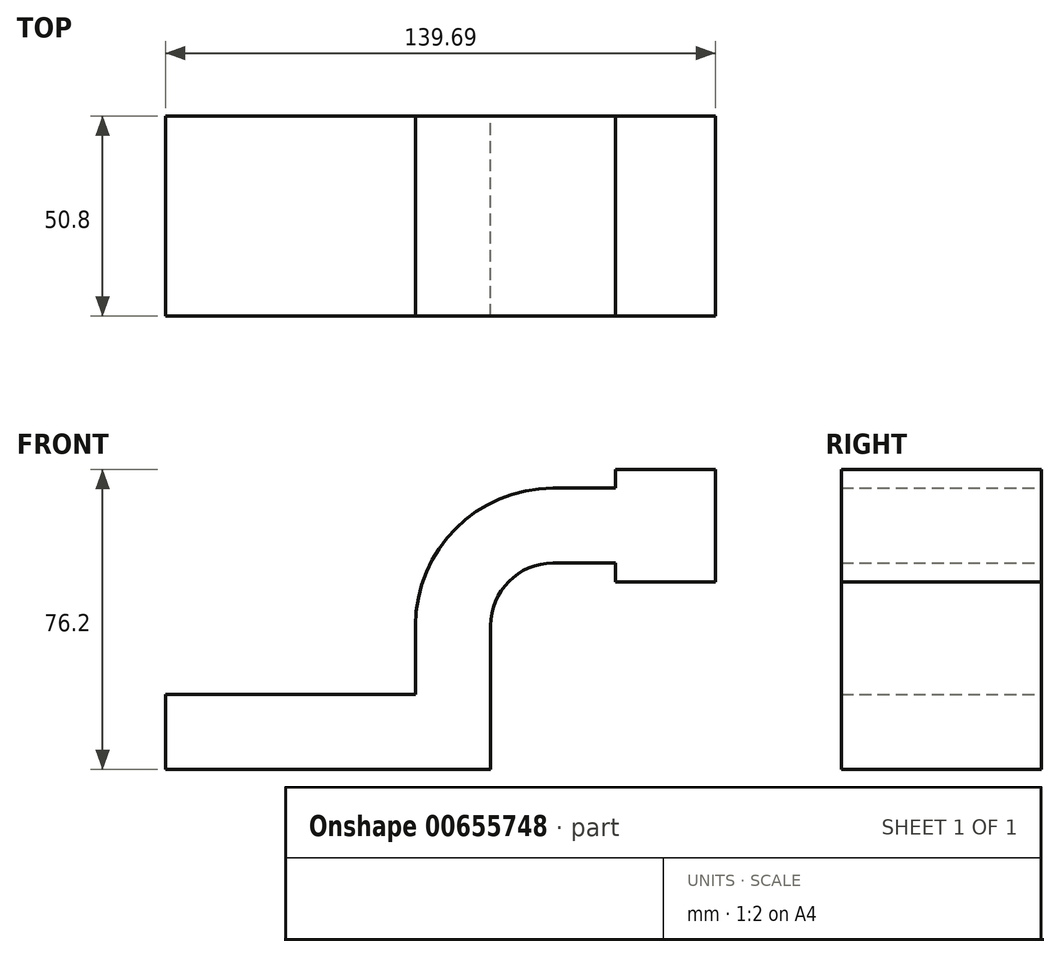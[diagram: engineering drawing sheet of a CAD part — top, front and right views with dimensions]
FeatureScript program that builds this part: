
annotation { "Feature Type Name" : "Feature", "Feature Type Description" : "" }
export const myFeature = defineFeature(function(context is Context, id is Id, definition is map)
    precondition{}
    {
        {
            var Q0;
            Q0=qCreatedBy(makeId("Front.planeOp"),FACE);
            var sketch = newSketch(context, id + "F0", { "sketchPlane" : qUnion([Q0])});
            skLineSegment(sketch, "E0.bottom", {"start": v(41.28, -9.52) * mm, "end": v(-41.28, -9.53) * mm});
            skLineSegment(sketch, "E0.top", {"start": v(41.28, 9.53) * mm, "end": v(-41.28, 9.53) * mm});
            skLineSegment(sketch, "E0.left", {"start": v(41.28, -9.52) * mm, "end": v(41.28, 9.53) * mm});
            skLineSegment(sketch, "E0.right", {"start": v(-41.28, -9.53) * mm, "end": v(-41.28, 9.53) * mm});
            skPoint(sketch, "E0.middle", {"position": v(0, 0) * mm});
            skLineSegment(sketch, "E1.bottom", {"start": v(98.43, 38.1) * mm, "end": v(73.03, 38.1) * mm});
            skLineSegment(sketch, "E1.top", {"start": v(98.43, 66.68) * mm, "end": v(73.03, 66.68) * mm});
            skLineSegment(sketch, "E1.left", {"start": v(98.43, 38.1) * mm, "end": v(98.43, 66.68) * mm});
            skLineSegment(sketch, "E1.right", {"start": v(73.03, 38.1) * mm, "end": v(73.03, 66.68) * mm});
            skPoint(sketch, "E1.middle", {"position": v(85.73, 52.39) * mm});
            skLineSegment(sketch, "E2", {"start": v(41.28, 9.53) * mm, "end": v(41.28, 27) * mm});
            skArc(sketch, "E3", {"start": v(41.27, 27) * mm, "mid": v(45.92, 38.23) * mm, "end": v(57.15, 42.88) * mm});
            skLineSegment(sketch, "E4", {"start": v(57.15, 42.88) * mm, "end": v(73.8, 42.88) * mm});
            skLineSegment(sketch, "E5.0", {"start": v(57.15, 43.1) * mm, "end": v(73.8, 43.1) * mm});
            skLineSegment(sketch, "E6.0", {"start": v(57.15, 61.93) * mm, "end": v(73.8, 61.93) * mm});
            skArc(sketch, "E6.1", {"start": v(22.22, 27) * mm, "mid": v(32.45, 51.7) * mm, "end": v(57.15, 61.93) * mm});
            skLineSegment(sketch, "E6.2", {"start": v(22.22, 9.53) * mm, "end": v(22.22, 27) * mm});
            skSolve(sketch);
        }
        {
            var Q0;
            Q0=makeQuery(id+"F0.imprint","IMPRINT",FACE,{"disambiguationData":[TD([[makeQuery(id+"F0.imprint","IMPRINT",EDGE,{"derivedFrom":sQuery(id+"F0.wireOp",EDGE,"E0.bottom")}),-1.0]])]});
            var Q1;
            {var subQ0=sQuery(id+"F0.wireOp",EDGE,"E2");Q1=makeQuery(id+"F0.imprint","IMPRINT",FACE,{"disambiguationData":[TD([[makeQuery(id+"F0.imprint","IMPRINT",EDGE,{"derivedFrom":subQ0}),1.0]])]});}
            var Q2;
            {var subQ1=sQuery(id+"F0.wireOp",EDGE,"E1.bottom");Q2=makeQuery(id+"F0.imprint","IMPRINT",FACE,{"disambiguationData":[TD([[makeQuery(id+"F0.imprint","IMPRINT",EDGE,{"derivedFrom":subQ1}),-1.0]])]});}
            extrude(context, id + "F1", {"entities" : qUnion([Q0, Q1, Q2]), "endBound" : BoundingType.SYMMETRIC, "depth" : 50.8 * mm, "offsetDistance" : 25.4 * mm});
        }
    });
